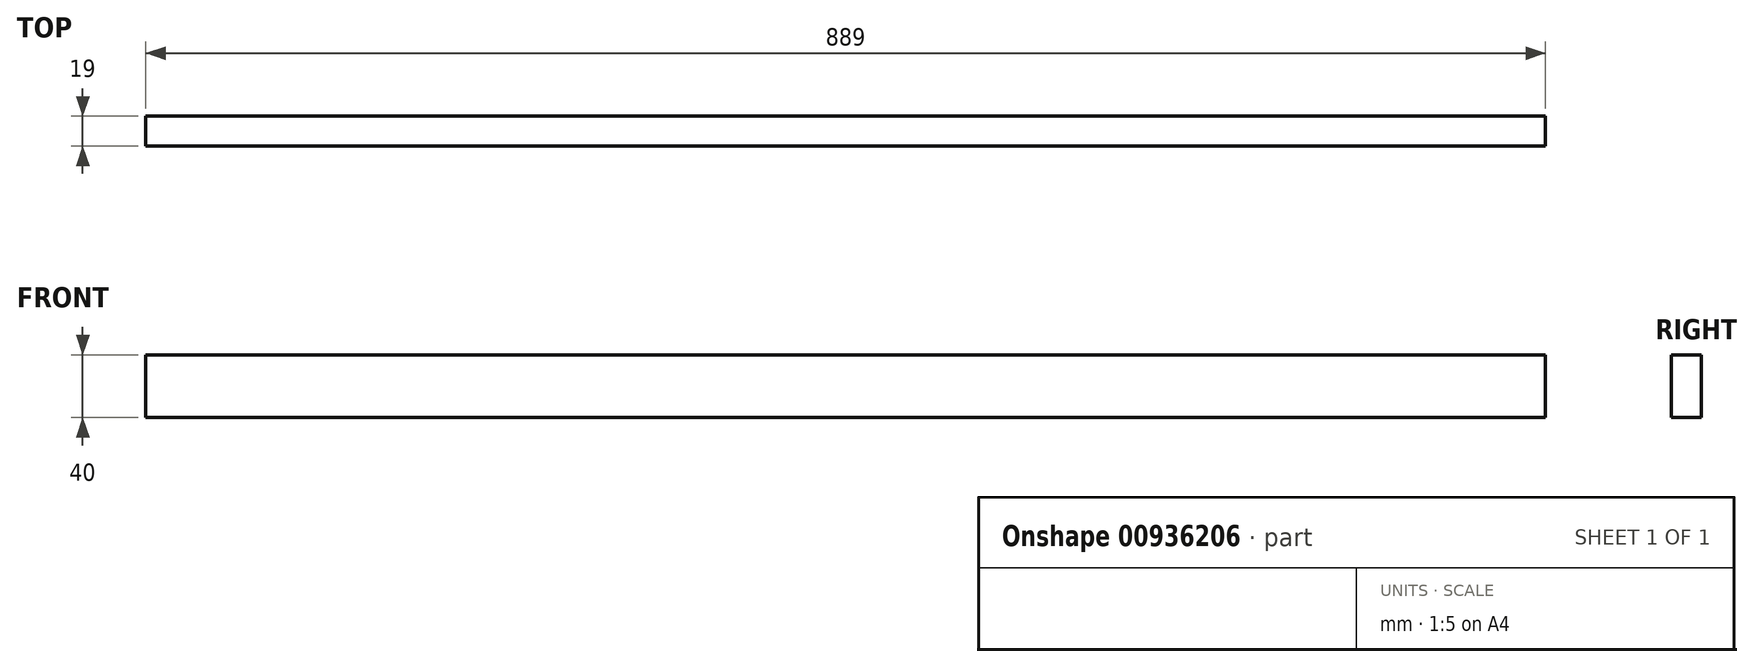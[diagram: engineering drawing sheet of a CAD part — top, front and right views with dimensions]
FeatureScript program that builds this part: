
annotation { "Feature Type Name" : "Feature", "Feature Type Description" : "" }
export const myFeature = defineFeature(function(context is Context, id is Id, definition is map)
    precondition{}
    {
        {
            var Q0;
            Q0=qCreatedBy(makeId("Right.planeOp"),FACE);
            var sketch = newSketch(context, id + "F0", { "sketchPlane" : qUnion([Q0])});
            skLineSegment(sketch, "E0.bottom", {"start": v(0, 0) * mm, "end": v(19, 0) * mm});
            skLineSegment(sketch, "E0.top", {"start": v(0, 40) * mm, "end": v(19, 40) * mm});
            skLineSegment(sketch, "E0.left", {"start": v(0, 0) * mm, "end": v(0, 40) * mm});
            skLineSegment(sketch, "E0.right", {"start": v(19, 0) * mm, "end": v(19, 40) * mm});
            skSolve(sketch);
        }
        {
            var Q0;
            Q0 = qSketchRegion(id + "F0", true);
            extrude(context, id + "F1", {"entities" : qUnion([Q0]), "depth" : 889 * mm, "offsetDistance" : 25 * mm});
        }
    });
